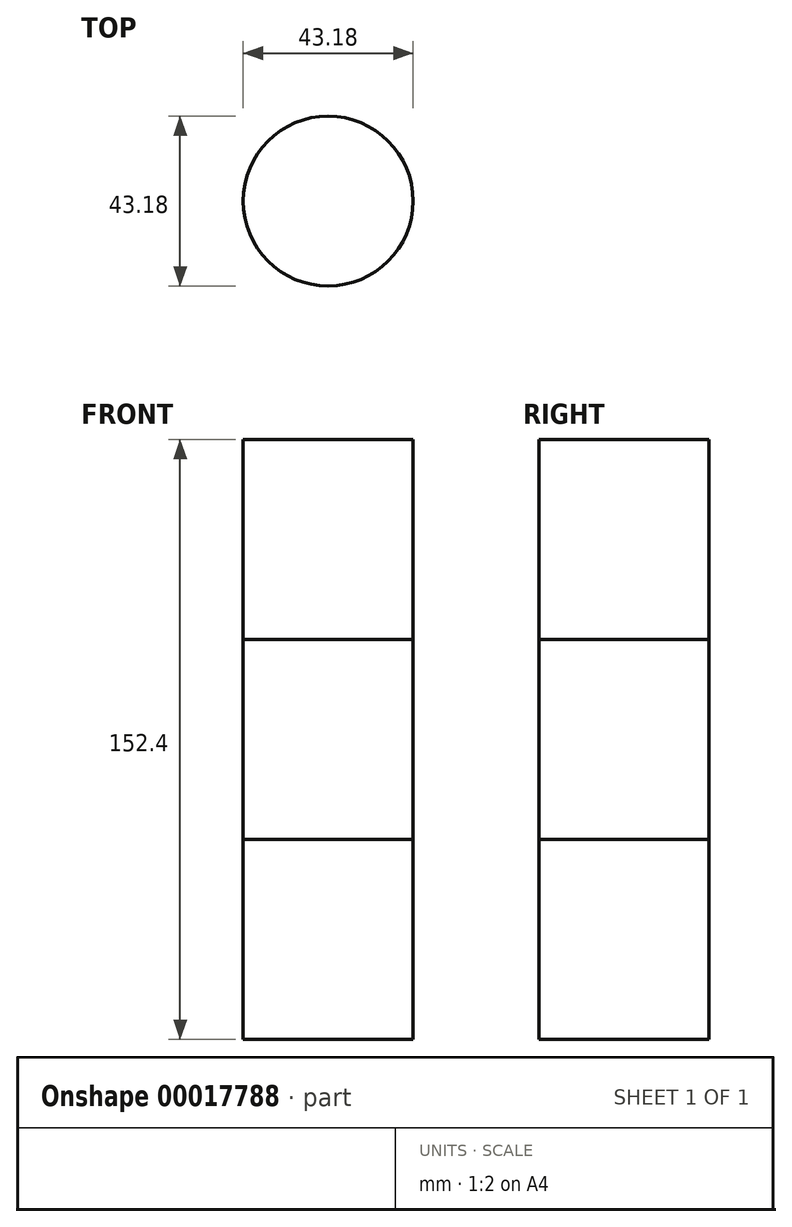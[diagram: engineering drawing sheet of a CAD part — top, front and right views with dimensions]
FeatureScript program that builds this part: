
annotation { "Feature Type Name" : "Feature", "Feature Type Description" : "" }
export const myFeature = defineFeature(function(context is Context, id is Id, definition is map)
    precondition{}
    {
        {
            var Q0;
            Q0=qCreatedBy(makeId("Top.planeOp"),FACE);
            var sketch = newSketch(context, id + "F0", { "sketchPlane" : qUnion([Q0])});
            skCircle(sketch, "E0", {"center": v(0, 0) * mm, "radius": 21.59 * mm});
            skSolve(sketch);
        }
        {
            var Q0;
            Q0=makeQuery(id+"F0.imprint","IMPRINT",FACE,{"disambiguationData":[TD([[makeQuery(id+"F0.imprint","IMPRINT",EDGE,{"derivedFrom":sQuery(id+"F0.wireOp",EDGE,"E0")}),1.0]])]});
            extrude(context, id + "F1", {"entities" : qUnion([Q0]), "depth" : 50.8 * mm});
        }
        {
            var Q0;
            Q0=makeQuery(id+"F1.opExtrude","CAP_FACE",FACE,{"disambiguationData":[OSD([sQuery(id+"F0.wireOp",EDGE,"E0")])],"isStart":false});
            extrude(context, id + "F2", {"entities" : qUnion([Q0]), "depth" : 50.8 * mm});
        }
        {
            var Q0;
            Q0=makeQuery(id+"F2.opExtrude","CAP_FACE",FACE,{"disambiguationData":[OSD([sQuery(id+"F0.wireOp",EDGE,"E0")])],"isStart":false});
            extrude(context, id + "F3", {"entities" : qUnion([Q0]), "depth" : 50.8 * mm});
        }
    });
